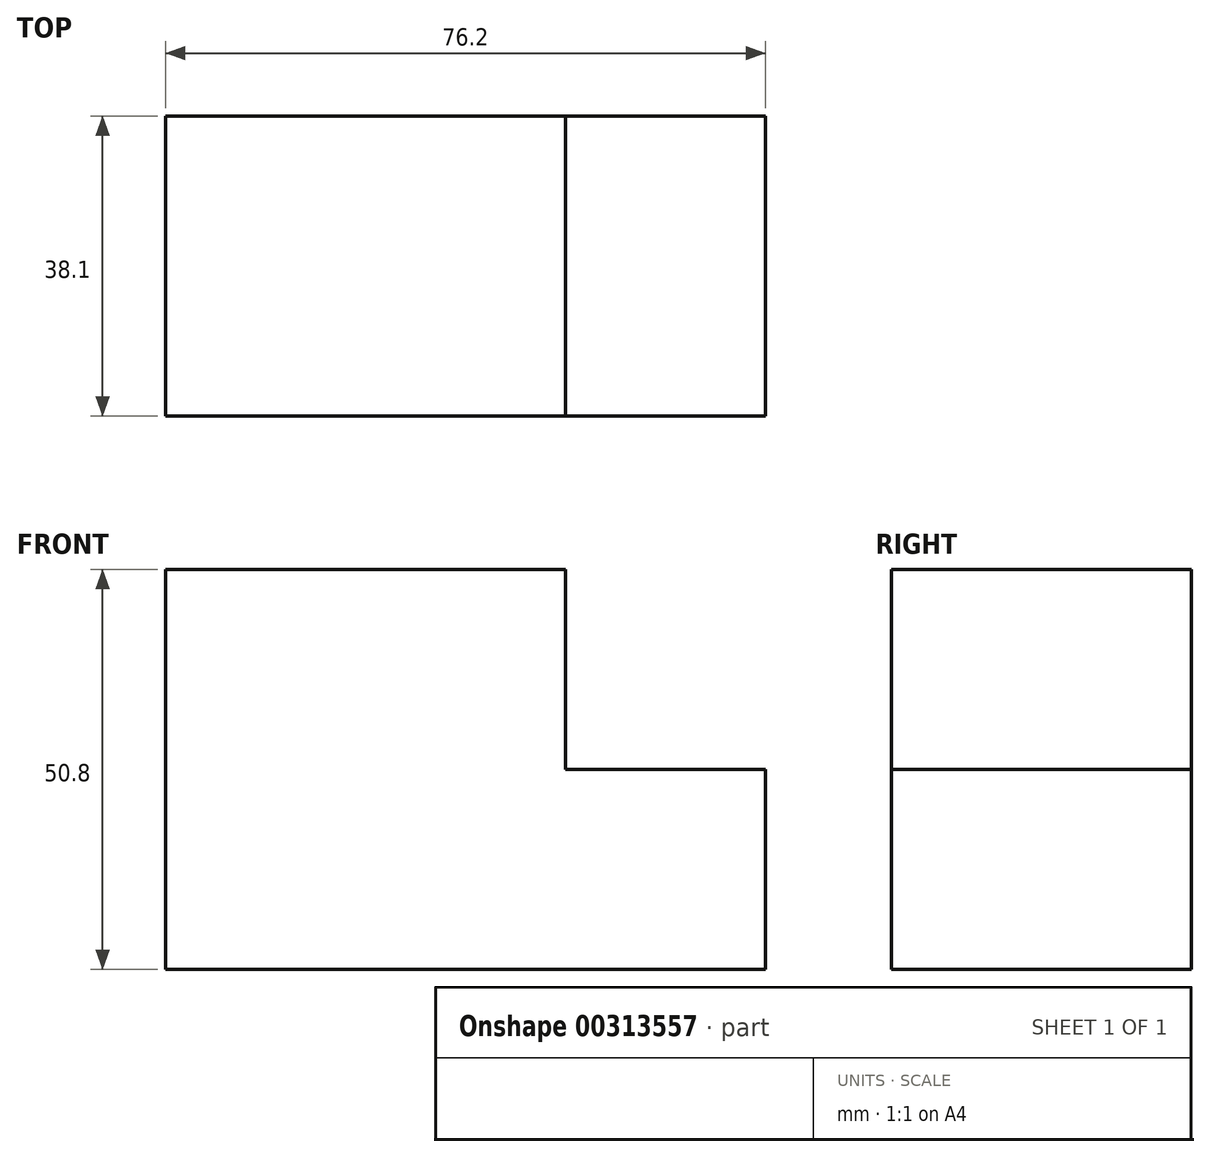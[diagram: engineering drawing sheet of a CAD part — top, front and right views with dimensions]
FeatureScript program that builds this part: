
annotation { "Feature Type Name" : "Feature", "Feature Type Description" : "" }
export const myFeature = defineFeature(function(context is Context, id is Id, definition is map)
    precondition{}
    {
        {
            var Q0;
            Q0=qCreatedBy(makeId("Front.planeOp"),FACE);
            var sketch = newSketch(context, id + "F0", { "sketchPlane" : qUnion([Q0])});
            skLineSegment(sketch, "E0", {"start": v(-33.15, -48.32) * mm, "end": v(43.05, -48.32) * mm});
            skLineSegment(sketch, "E1", {"start": v(43.05, -48.32) * mm, "end": v(43.05, -22.92) * mm});
            skLineSegment(sketch, "E2", {"start": v(43.05, -22.92) * mm, "end": v(17.65, -22.92) * mm});
            skLineSegment(sketch, "E3", {"start": v(17.65, -22.92) * mm, "end": v(17.65, 2.48) * mm});
            skLineSegment(sketch, "E4", {"start": v(17.65, 2.48) * mm, "end": v(-33.15, 2.48) * mm});
            skLineSegment(sketch, "E5", {"start": v(-33.15, 2.48) * mm, "end": v(-33.15, -48.32) * mm});
            skSolve(sketch);
        }
        {
            var Q0;
            Q0=makeQuery(id+"F0.imprint","IMPRINT",FACE,{"disambiguationData":[TD([[makeQuery(id+"F0.imprint","IMPRINT",EDGE,{"derivedFrom":sQuery(id+"F0.wireOp",EDGE,"E0")}),1.0]])]});
            var sketch = newSketch(context, id + "F1", { "sketchPlane" : qUnion([Q0])});
            skSolve(sketch);
        }
        {
            var Q0;
            Q0 = qSketchRegion(id + "F1", true);
            var Q1;
            Q1=makeQuery(id+"F0.imprint","IMPRINT",FACE,{"disambiguationData":[TD([[makeQuery(id+"F0.imprint","IMPRINT",EDGE,{"derivedFrom":sQuery(id+"F0.wireOp",EDGE,"E0")}),1.0]])]});
            extrude(context, id + "F2", {"entities" : qUnion([Q0, Q1]), "depth" : 38.1 * mm});
        }
    });
